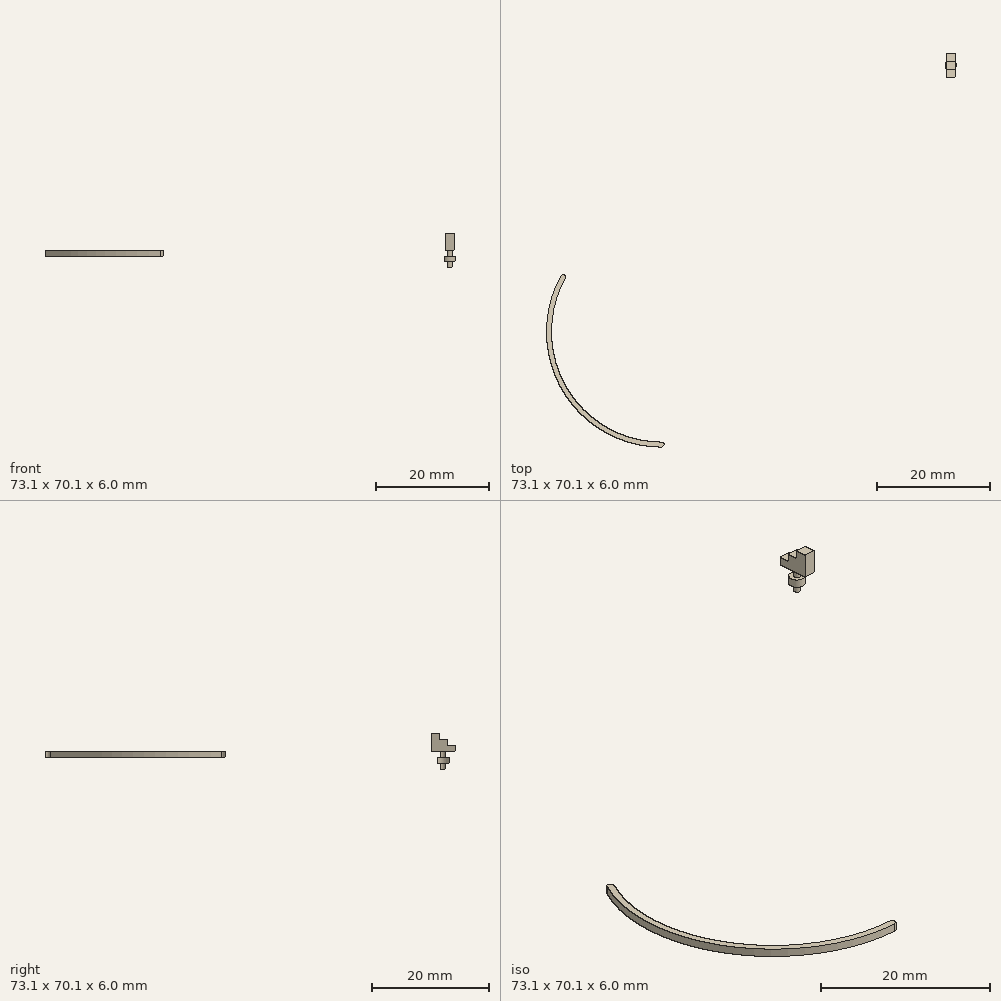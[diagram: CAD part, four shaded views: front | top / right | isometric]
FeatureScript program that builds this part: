
annotation { "Feature Type Name" : "Feature", "Feature Type Description" : "" }
export const myFeature = defineFeature(function(context is Context, id is Id, definition is map)
    precondition{}
    {
        {
            var Q0;
            Q0=qCreatedBy(makeId("Top.planeOp"),FACE);
            var sketch = newSketch(context, id + "F0", { "sketchPlane" : qUnion([Q0])});
            skCircle(sketch, "E0", {"center": v(0, 0) * mm, "radius": 35 * mm});
            skArc(sketch, "E1", {"start": v(0, -3.01) * mm, "mid": v(-17.68, 7.1) * mm, "end": v(-17.92, 27.47) * mm});
            skPoint(sketch, "E1.startSnap0", {"position": v(0, 17.5) * mm});
            skLineSegment(sketch, "E2.trimOffspring", {"start": v(0, 32.8) * mm, "end": v(0, 35) * mm});
            skArc(sketch, "E3.0", {"start": v(0, -2.11) * mm, "mid": v(-16.9, 7.56) * mm, "end": v(-17.14, 27.04) * mm});
            skArc(sketch, "E4", {"start": v(-17.92, 27.47) * mm, "mid": v(-17.31, 27.65) * mm, "end": v(-17.14, 27.04) * mm});
            skArc(sketch, "E5", {"start": v(0, -3.01) * mm, "mid": v(0.45, -2.56) * mm, "end": v(0, -2.11) * mm});
            skArc(sketch, "E6.1.0", {"start": v(2, -0.65) * mm, "mid": v(-12.41, -13.74) * mm, "end": v(-31, -7.94) * mm});
            skArc(sketch, "E6.1.1", {"start": v(2.86, -0.93) * mm, "mid": v(-12.22, -14.62) * mm, "end": v(-31.67, -8.56) * mm});
            skArc(sketch, "E6.1.2", {"start": v(2.86, -0.93) * mm, "mid": v(2.58, -0.36) * mm, "end": v(2, -0.65) * mm});
            skArc(sketch, "E6.1.3", {"start": v(-31.67, -8.56) * mm, "mid": v(-31.64, -7.92) * mm, "end": v(-31, -7.94) * mm});
            skArc(sketch, "E6.2.0", {"start": v(1.24, 1.7) * mm, "mid": v(9.23, -16.05) * mm, "end": v(-2.03, -31.95) * mm});
            skArc(sketch, "E6.2.1", {"start": v(1.77, 2.44) * mm, "mid": v(10.13, -16.14) * mm, "end": v(-1.65, -32.76) * mm});
            skArc(sketch, "E6.2.2", {"start": v(1.77, 2.44) * mm, "mid": v(1.14, 2.34) * mm, "end": v(1.24, 1.7) * mm});
            skArc(sketch, "E6.2.3", {"start": v(-1.65, -32.76) * mm, "mid": v(-2.25, -32.54) * mm, "end": v(-2.03, -31.95) * mm});
            skArc(sketch, "E6.3.0", {"start": v(-1.24, 1.7) * mm, "mid": v(18.12, 3.82) * mm, "end": v(29.76, -11.8) * mm});
            skArc(sketch, "E6.3.1", {"start": v(-1.77, 2.44) * mm, "mid": v(18.48, 4.65) * mm, "end": v(30.65, -11.7) * mm});
            skArc(sketch, "E6.3.2", {"start": v(-1.77, 2.44) * mm, "mid": v(-1.87, 1.8) * mm, "end": v(-1.24, 1.7) * mm});
            skArc(sketch, "E6.3.3", {"start": v(30.65, -11.7) * mm, "mid": v(30.26, -12.2) * mm, "end": v(29.76, -11.8) * mm});
            skArc(sketch, "E6.4.0", {"start": v(-2, -0.65) * mm, "mid": v(1.97, 18.41) * mm, "end": v(20.42, 24.65) * mm});
            skArc(sketch, "E6.4.1", {"start": v(-2.86, -0.93) * mm, "mid": v(1.3, 19.01) * mm, "end": v(20.6, 25.54) * mm});
            skArc(sketch, "E6.4.2", {"start": v(-2.86, -0.93) * mm, "mid": v(-2.3, -1.22) * mm, "end": v(-2, -0.65) * mm});
            skArc(sketch, "E6.4.3", {"start": v(20.6, 25.54) * mm, "mid": v(20.95, 25) * mm, "end": v(20.42, 24.65) * mm});
            skSolve(sketch);
        }
        {
            var Q0;
            Q0=makeQuery(id+"F0.imprint","IMPRINT",FACE,{"disambiguationData":[TD([[makeQuery(id+"F0.imprint","IMPRINT",EDGE,{"derivedFrom":sQuery(id+"F0.wireOp",EDGE,"E1")}),1.0]])]});
            extrude(context, id + "F1", {"entities" : qUnion([Q0]), "depth" : 1 * mm, "offsetDistance" : 25 * mm});
        }
        {
            var Q0;
            Q0=qCreatedBy(makeId("Top.planeOp"),FACE);
            var Q1;
            Q1=qCreatedBy(makeId("Top.planeOp"),FACE);
            var Q2;
            Q2=qCreatedBy(makeId("Top.planeOp"),FACE);
            var Q3;
            Q3=qCreatedBy(makeId("Top.planeOp"),FACE);
            var sketch = newSketch(context, id + "F2", { "sketchPlane" : qUnion([Q0, Q1, Q2, Q3])});
            skCircle(sketch, "E7", {"center": v(51.56, 64.99) * mm, "radius": 0.45 * mm});
            skCircle(sketch, "E8", {"center": v(51.56, 64.99) * mm, "radius": 1 * mm});
            skSolve(sketch);
        }
        {
            var Q0;
            Q0 = qSketchRegion(id + "F2", true);
            var Q1;
            Q1=makeQuery(id+"F2.imprint","IMPRINT",FACE,{"disambiguationData":[TD([[makeQuery(id+"F2.imprint","IMPRINT",EDGE,{"derivedFrom":sQuery(id+"F2.wireOp",EDGE,"E7")}),1.0]])]});
            extrude(context, id + "F3", {"entities" : qUnion([Q0, Q1]), "oppositeDirection" : true, "depth" : 1 * mm, "offsetDistance" : 25 * mm});
        }
        {
            var Q0;
            Q0=makeQuery(id+"F2.imprint","IMPRINT",FACE,{"disambiguationData":[TD([[makeQuery(id+"F2.imprint","IMPRINT",EDGE,{"derivedFrom":sQuery(id+"F2.wireOp",EDGE,"E7")}),1.0]])]});
            extrude(context, id + "F4", {"entities" : qUnion([Q0]), "operationType" : NewBodyOperationType.ADD, "depth" : 1 * mm, "offsetDistance" : 25 * mm});
        }
        {
            var Q0;
            Q0=makeQuery(id+"F4.opExtrude","CAP_FACE",FACE,{"disambiguationData":[OSD([sQuery(id+"F2.wireOp",EDGE,"E7")])],"isStart":false});
            var sketch = newSketch(context, id + "F5", { "sketchPlane" : qUnion([Q0])});
            skLineSegment(sketch, "E9.bottom", {"start": v(52.33, 67.08) * mm, "end": v(50.78, 67.08) * mm});
            skLineSegment(sketch, "E9.top", {"start": v(52.33, 62.9) * mm, "end": v(50.78, 62.9) * mm});
            skLineSegment(sketch, "E9.left", {"start": v(52.33, 67.08) * mm, "end": v(52.33, 62.9) * mm});
            skLineSegment(sketch, "E9.right", {"start": v(50.78, 67.08) * mm, "end": v(50.78, 62.9) * mm});
            skPoint(sketch, "E9.middle", {"position": v(51.56, 64.99) * mm});
            skLineSegment(sketch, "E10.bottom", {"start": v(52.33, 65.68) * mm, "end": v(50.78, 65.68) * mm});
            skLineSegment(sketch, "E10.top", {"start": v(52.33, 64.29) * mm, "end": v(50.78, 64.29) * mm});
            skLineSegment(sketch, "E10.left", {"start": v(52.33, 65.68) * mm, "end": v(52.33, 64.29) * mm});
            skLineSegment(sketch, "E10.right", {"start": v(50.78, 65.68) * mm, "end": v(50.78, 64.29) * mm});
            skSolve(sketch);
        }
        {
            var Q0;
            Q0=makeQuery(id+"F5.imprint","IMPRINT",FACE,{"disambiguationData":[TD([[makeQuery(id+"F5.imprint","IMPRINT",EDGE,{"derivedFrom":sQuery(id+"F5.wireOp",EDGE,"E10.bottom")}),1.0]])]});
            var Q1;
            Q1=makeQuery(id+"F5.imprint","IMPRINT",FACE,{"disambiguationData":[TD([[makeQuery(id+"F5.imprint","IMPRINT",EDGE,{"derivedFrom":makeQuery(id+"F4.opExtrude","CAP_EDGE",EDGE,{"disambiguationData":[OSD([sQuery(id+"F2.wireOp",EDGE,"E7")])],"isStart":false})}),1.0]])]});
            extrude(context, id + "F6", {"entities" : qUnion([Q0, Q1]), "operationType" : NewBodyOperationType.ADD, "depth" : 2 * mm, "offsetDistance" : 25 * mm});
        }
        {
            var Q0;
            {var subQ0=sQuery(id+"F5.wireOp",EDGE,"E9.bottom");Q0=makeQuery(id+"F5.imprint","IMPRINT",FACE,{"disambiguationData":[TD([[makeQuery(id+"F5.imprint","IMPRINT",EDGE,{"derivedFrom":subQ0}),1.0]])]});}
            extrude(context, id + "F7", {"entities" : qUnion([Q0]), "operationType" : NewBodyOperationType.ADD, "depth" : 1 * mm, "offsetDistance" : 25 * mm});
        }
        {
            var Q0;
            {var subQ0=sQuery(id+"F5.wireOp",EDGE,"E9.top");Q0=makeQuery(id+"F5.imprint","IMPRINT",FACE,{"disambiguationData":[TD([[makeQuery(id+"F5.imprint","IMPRINT",EDGE,{"derivedFrom":subQ0}),-1.0]])]});}
            extrude(context, id + "F8", {"entities" : qUnion([Q0]), "operationType" : NewBodyOperationType.ADD, "depth" : 3 * mm, "offsetDistance" : 25 * mm});
        }
        {
            var Q0;
            Q0=makeQuery(id+"F3.opExtrude","CAP_FACE",FACE,{"disambiguationData":[OSD([sQuery(id+"F2.wireOp",EDGE,"E8")])],"isStart":false});
            var sketch = newSketch(context, id + "F9", { "sketchPlane" : qUnion([Q0])});
            skCircle(sketch, "E11", {"center": v(51.56, -64.99) * mm, "radius": 0.45 * mm});
            skSolve(sketch);
        }
        {
            var Q0;
            Q0=makeQuery(id+"F9.imprint","IMPRINT",FACE,{"disambiguationData":[TD([[makeQuery(id+"F9.imprint","IMPRINT",EDGE,{"derivedFrom":sQuery(id+"F9.wireOp",EDGE,"E11")}),1.0]])]});
            extrude(context, id + "F10", {"entities" : qUnion([Q0]), "operationType" : NewBodyOperationType.ADD, "depth" : 1 * mm, "offsetDistance" : 25 * mm});
        }
    });
